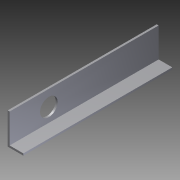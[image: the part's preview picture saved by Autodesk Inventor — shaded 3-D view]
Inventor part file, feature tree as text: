
AUTODESK INVENTOR PART (.ipt)
format: ipt  version: 2012 (Build 160160000, 160)  size: 88,064 bytes
history: native  units: in
note: dims shown in document units (in); Inventor stores cm internally (conversion verified against a paired STEP export)
features: extrude x2, sketch x2
ambient origin geometry x8: Origin, YZ Plane, XZ Plane, XY Plane, X Axis, Y Axis, Z Axis, Center Point
bodies: Solid1 (feature_tree)
feature tree (4):
  extrude  "Extrusion1"  Depth=1.0in
  extrude  "Extrusion2"  Depth=0.125in
  sketch  "Sketch1"  dims[d0=2.0in d1=1.0in]
  sketch  "Sketch2"  dims[d2=0.125in d3=0.125in d4=9.5in d5=0.0in d6=1.125in d8=1.0in d9=4.0in d10=0.0in d11=2.5in]
